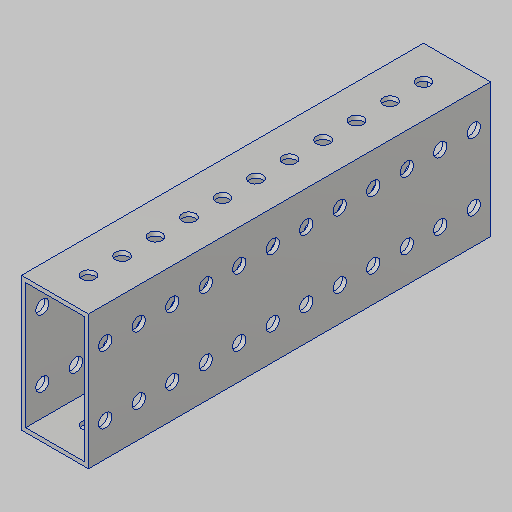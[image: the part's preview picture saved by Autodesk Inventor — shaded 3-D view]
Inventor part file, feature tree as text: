
AUTODESK INVENTOR PART (.ipt)
format: ipt  version: 2023.5 (Build 275446000, 446)  size: 214,016 bytes
history: native  units: in
note: dims shown in document units (in); Inventor stores cm internally (conversion verified against a paired STEP export)
features: hole x2, sketch x2, projected_geometry x2, extrude x1
ambient origin geometry x8: Origin, YZ Plane, XZ Plane, XY Plane, X Axis, Y Axis, Z Axis, Center Point
bodies: Solid1 (feature_tree)
feature tree (7):
  extrude  "Extrusion1"  Depth=0.5in
  hole  "Hole1"  [1 undecoded]
  hole  "Hole2"  [1 undecoded]
  sketch  "Sketch2"  dims[d4=0.0in d5=0.5in]
  projected_geometry  "Projected Loop1"
  sketch  "Sketch3"  dims[d6=4.3307in d8=0.5in d9=0.3937in d11=1.0in d13=0.201in d14=0.75in d15=0.375in d16=0.19in d17=0.5635in d18=1.0in d19=0.8108in d20=1.0in d21=0.25in d22=4.7244in d24=0.5in d25=0.3937in d27=1.0in d29=0.201in d30=0.75in d31=0.375in d32=0.25in d33=0.5635in d34=1.0in d35=0.8108in]
  projected_geometry  "Projected Loop2"
note: 2 required parameter values undecoded (feature->parameter linkage not recoverable at this tier; creation-order binding heuristic only, values carry confidence <= 0.55)
